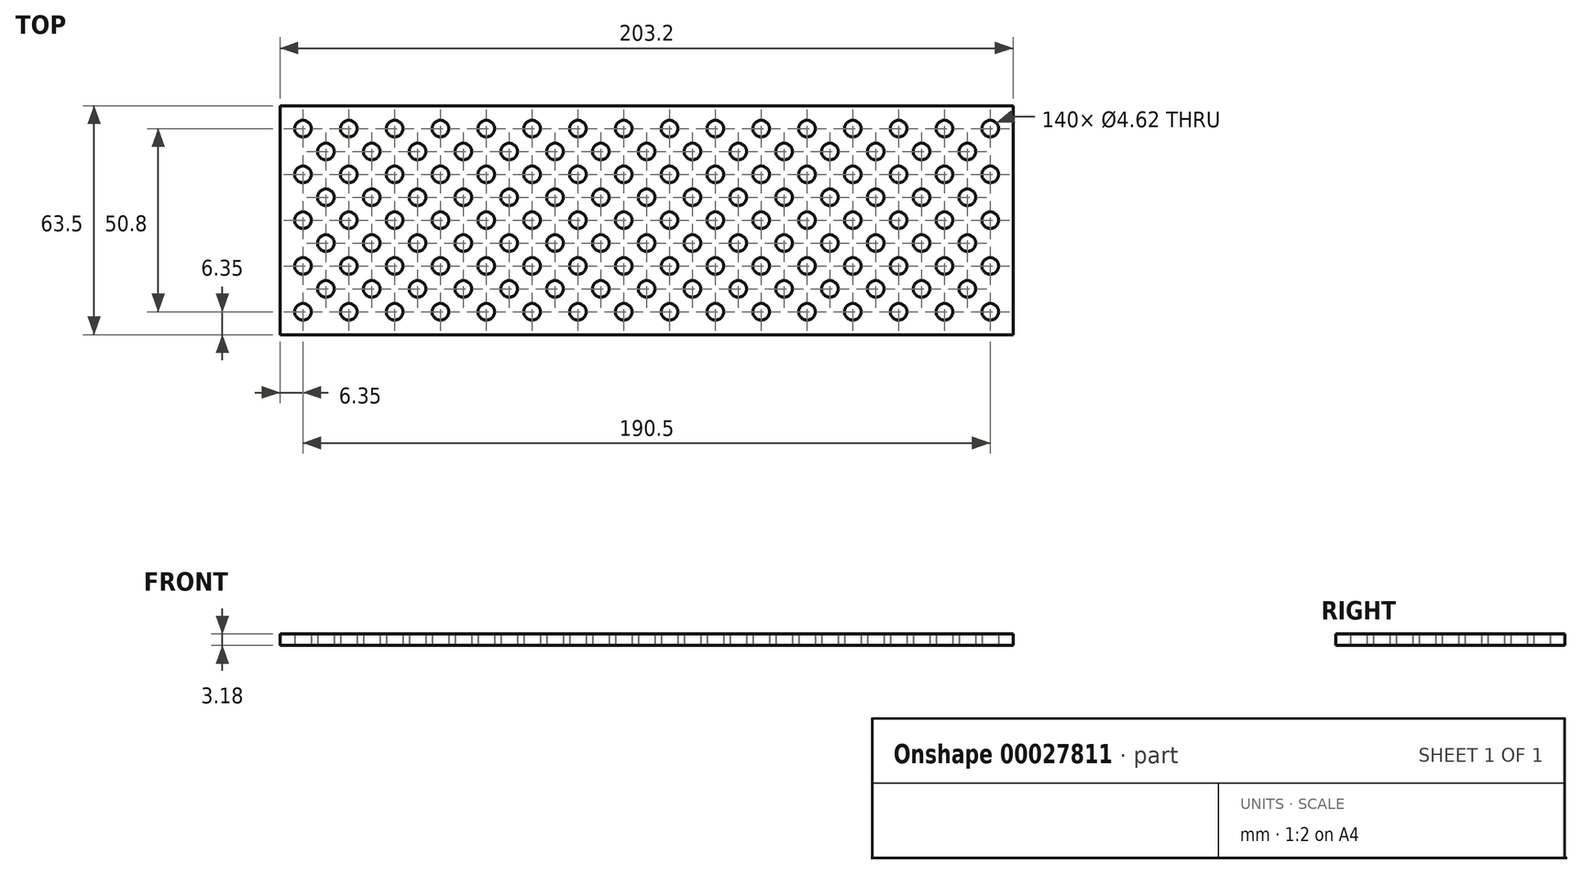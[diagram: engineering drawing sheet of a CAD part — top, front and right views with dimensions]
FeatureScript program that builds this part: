
annotation { "Feature Type Name" : "Feature", "Feature Type Description" : "" }
export const myFeature = defineFeature(function(context is Context, id is Id, definition is map)
    precondition{}
    {
        {
            var Q0;
            Q0=qCreatedBy(makeId("Top.planeOp"),FACE);
            var sketch = newSketch(context, id + "F0", { "sketchPlane" : qUnion([Q0])});
            skLineSegment(sketch, "E0.bottom", {"start": v(0, 0) * mm, "end": v(203.2, 0) * mm});
            skLineSegment(sketch, "E0.top", {"start": v(0, 63.5) * mm, "end": v(203.2, 63.5) * mm});
            skLineSegment(sketch, "E0.left", {"start": v(0, 0) * mm, "end": v(0, 63.5) * mm});
            skLineSegment(sketch, "E0.right", {"start": v(203.2, 0) * mm, "end": v(203.2, 63.5) * mm});
            skPoint(sketch, "E1", {"position": v(4.04, 4.04) * mm});
            skCircle(sketch, "E2", {"center": v(6.35, 6.35) * mm, "radius": 2.31 * mm});
            skCircle(sketch, "E3.0.1.0", {"center": v(6.35, 19.05) * mm, "radius": 2.31 * mm});
            skCircle(sketch, "E3.0.2.0", {"center": v(6.35, 31.75) * mm, "radius": 2.31 * mm});
            skCircle(sketch, "E3.0.3.0", {"center": v(6.35, 44.45) * mm, "radius": 2.31 * mm});
            skCircle(sketch, "E3.0.4.0", {"center": v(6.35, 57.15) * mm, "radius": 2.31 * mm});
            skCircle(sketch, "E3.1.0.0", {"center": v(19.05, 6.35) * mm, "radius": 2.31 * mm});
            skCircle(sketch, "E3.1.1.0", {"center": v(19.05, 19.05) * mm, "radius": 2.31 * mm});
            skCircle(sketch, "E3.1.2.0", {"center": v(19.05, 31.75) * mm, "radius": 2.31 * mm});
            skCircle(sketch, "E3.1.3.0", {"center": v(19.05, 44.45) * mm, "radius": 2.31 * mm});
            skCircle(sketch, "E3.1.4.0", {"center": v(19.05, 57.15) * mm, "radius": 2.31 * mm});
            skCircle(sketch, "E3.2.0.0", {"center": v(31.75, 6.35) * mm, "radius": 2.31 * mm});
            skCircle(sketch, "E3.2.1.0", {"center": v(31.75, 19.05) * mm, "radius": 2.31 * mm});
            skCircle(sketch, "E3.2.2.0", {"center": v(31.75, 31.75) * mm, "radius": 2.31 * mm});
            skCircle(sketch, "E3.2.3.0", {"center": v(31.75, 44.45) * mm, "radius": 2.31 * mm});
            skCircle(sketch, "E3.2.4.0", {"center": v(31.75, 57.15) * mm, "radius": 2.31 * mm});
            skCircle(sketch, "E3.3.0.0", {"center": v(44.45, 6.35) * mm, "radius": 2.31 * mm});
            skCircle(sketch, "E3.3.1.0", {"center": v(44.45, 19.05) * mm, "radius": 2.31 * mm});
            skCircle(sketch, "E3.3.2.0", {"center": v(44.45, 31.75) * mm, "radius": 2.31 * mm});
            skCircle(sketch, "E3.3.3.0", {"center": v(44.45, 44.45) * mm, "radius": 2.31 * mm});
            skCircle(sketch, "E3.3.4.0", {"center": v(44.45, 57.15) * mm, "radius": 2.31 * mm});
            skCircle(sketch, "E3.4.0.0", {"center": v(57.15, 6.35) * mm, "radius": 2.31 * mm});
            skCircle(sketch, "E3.4.1.0", {"center": v(57.15, 19.05) * mm, "radius": 2.31 * mm});
            skCircle(sketch, "E3.4.2.0", {"center": v(57.15, 31.75) * mm, "radius": 2.31 * mm});
            skCircle(sketch, "E3.4.3.0", {"center": v(57.15, 44.45) * mm, "radius": 2.31 * mm});
            skCircle(sketch, "E3.4.4.0", {"center": v(57.15, 57.15) * mm, "radius": 2.31 * mm});
            skCircle(sketch, "E3.5.0.0", {"center": v(69.85, 6.35) * mm, "radius": 2.31 * mm});
            skCircle(sketch, "E3.5.1.0", {"center": v(69.85, 19.05) * mm, "radius": 2.31 * mm});
            skCircle(sketch, "E3.5.2.0", {"center": v(69.85, 31.75) * mm, "radius": 2.31 * mm});
            skCircle(sketch, "E3.5.3.0", {"center": v(69.85, 44.45) * mm, "radius": 2.31 * mm});
            skCircle(sketch, "E3.5.4.0", {"center": v(69.85, 57.15) * mm, "radius": 2.31 * mm});
            skCircle(sketch, "E3.6.0.0", {"center": v(82.55, 6.35) * mm, "radius": 2.31 * mm});
            skCircle(sketch, "E3.6.1.0", {"center": v(82.55, 19.05) * mm, "radius": 2.31 * mm});
            skCircle(sketch, "E3.6.2.0", {"center": v(82.55, 31.75) * mm, "radius": 2.31 * mm});
            skCircle(sketch, "E3.6.3.0", {"center": v(82.55, 44.45) * mm, "radius": 2.31 * mm});
            skCircle(sketch, "E3.6.4.0", {"center": v(82.55, 57.15) * mm, "radius": 2.31 * mm});
            skCircle(sketch, "E3.7.0.0", {"center": v(95.25, 6.35) * mm, "radius": 2.31 * mm});
            skCircle(sketch, "E3.7.1.0", {"center": v(95.25, 19.05) * mm, "radius": 2.31 * mm});
            skCircle(sketch, "E3.7.2.0", {"center": v(95.25, 31.75) * mm, "radius": 2.31 * mm});
            skCircle(sketch, "E3.7.3.0", {"center": v(95.25, 44.45) * mm, "radius": 2.31 * mm});
            skCircle(sketch, "E3.7.4.0", {"center": v(95.25, 57.15) * mm, "radius": 2.31 * mm});
            skCircle(sketch, "E3.8.0.0", {"center": v(107.95, 6.35) * mm, "radius": 2.31 * mm});
            skCircle(sketch, "E3.8.1.0", {"center": v(107.95, 19.05) * mm, "radius": 2.31 * mm});
            skCircle(sketch, "E3.8.2.0", {"center": v(107.95, 31.75) * mm, "radius": 2.31 * mm});
            skCircle(sketch, "E3.8.3.0", {"center": v(107.95, 44.45) * mm, "radius": 2.31 * mm});
            skCircle(sketch, "E3.8.4.0", {"center": v(107.95, 57.15) * mm, "radius": 2.31 * mm});
            skCircle(sketch, "E3.9.0.0", {"center": v(120.65, 6.35) * mm, "radius": 2.31 * mm});
            skCircle(sketch, "E3.9.1.0", {"center": v(120.65, 19.05) * mm, "radius": 2.31 * mm});
            skCircle(sketch, "E3.9.2.0", {"center": v(120.65, 31.75) * mm, "radius": 2.31 * mm});
            skCircle(sketch, "E3.9.3.0", {"center": v(120.65, 44.45) * mm, "radius": 2.31 * mm});
            skCircle(sketch, "E3.9.4.0", {"center": v(120.65, 57.15) * mm, "radius": 2.31 * mm});
            skCircle(sketch, "E3.10.0.0", {"center": v(133.35, 6.35) * mm, "radius": 2.31 * mm});
            skCircle(sketch, "E3.10.1.0", {"center": v(133.35, 19.05) * mm, "radius": 2.31 * mm});
            skCircle(sketch, "E3.10.2.0", {"center": v(133.35, 31.75) * mm, "radius": 2.31 * mm});
            skCircle(sketch, "E3.10.3.0", {"center": v(133.35, 44.45) * mm, "radius": 2.31 * mm});
            skCircle(sketch, "E3.10.4.0", {"center": v(133.35, 57.15) * mm, "radius": 2.31 * mm});
            skCircle(sketch, "E3.11.0.0", {"center": v(146.05, 6.35) * mm, "radius": 2.31 * mm});
            skCircle(sketch, "E3.11.1.0", {"center": v(146.05, 19.05) * mm, "radius": 2.31 * mm});
            skCircle(sketch, "E3.11.2.0", {"center": v(146.05, 31.75) * mm, "radius": 2.31 * mm});
            skCircle(sketch, "E3.11.3.0", {"center": v(146.05, 44.45) * mm, "radius": 2.31 * mm});
            skCircle(sketch, "E3.11.4.0", {"center": v(146.05, 57.15) * mm, "radius": 2.31 * mm});
            skCircle(sketch, "E3.12.0.0", {"center": v(158.75, 6.35) * mm, "radius": 2.31 * mm});
            skCircle(sketch, "E3.12.1.0", {"center": v(158.75, 19.05) * mm, "radius": 2.31 * mm});
            skCircle(sketch, "E3.12.2.0", {"center": v(158.75, 31.75) * mm, "radius": 2.31 * mm});
            skCircle(sketch, "E3.12.3.0", {"center": v(158.75, 44.45) * mm, "radius": 2.31 * mm});
            skCircle(sketch, "E3.12.4.0", {"center": v(158.75, 57.15) * mm, "radius": 2.31 * mm});
            skCircle(sketch, "E3.13.0.0", {"center": v(171.45, 6.35) * mm, "radius": 2.31 * mm});
            skCircle(sketch, "E3.13.1.0", {"center": v(171.45, 19.05) * mm, "radius": 2.31 * mm});
            skCircle(sketch, "E3.13.2.0", {"center": v(171.45, 31.75) * mm, "radius": 2.31 * mm});
            skCircle(sketch, "E3.13.3.0", {"center": v(171.45, 44.45) * mm, "radius": 2.31 * mm});
            skCircle(sketch, "E3.13.4.0", {"center": v(171.45, 57.15) * mm, "radius": 2.31 * mm});
            skCircle(sketch, "E3.14.0.0", {"center": v(184.15, 6.35) * mm, "radius": 2.31 * mm});
            skCircle(sketch, "E3.14.1.0", {"center": v(184.15, 19.05) * mm, "radius": 2.31 * mm});
            skCircle(sketch, "E3.14.2.0", {"center": v(184.15, 31.75) * mm, "radius": 2.31 * mm});
            skCircle(sketch, "E3.14.3.0", {"center": v(184.15, 44.45) * mm, "radius": 2.31 * mm});
            skCircle(sketch, "E3.14.4.0", {"center": v(184.15, 57.15) * mm, "radius": 2.31 * mm});
            skCircle(sketch, "E3.15.0.0", {"center": v(196.85, 6.35) * mm, "radius": 2.31 * mm});
            skCircle(sketch, "E3.15.1.0", {"center": v(196.85, 19.05) * mm, "radius": 2.31 * mm});
            skCircle(sketch, "E3.15.2.0", {"center": v(196.85, 31.75) * mm, "radius": 2.31 * mm});
            skCircle(sketch, "E3.15.3.0", {"center": v(196.85, 44.45) * mm, "radius": 2.31 * mm});
            skCircle(sketch, "E3.15.4.0", {"center": v(196.85, 57.15) * mm, "radius": 2.31 * mm});
            skLineSegment(sketch, "E3.direction1", {"start": v(6.35, 6.35) * mm, "end": v(19.05, 6.35) * mm, "construction": true});
            skLineSegment(sketch, "E3.direction2", {"start": v(6.35, 6.35) * mm, "end": v(6.35, 19.05) * mm, "construction": true});
            skCircle(sketch, "E4", {"center": v(12.7, 12.7) * mm, "radius": 2.31 * mm});
            skCircle(sketch, "E5.0.1.0", {"center": v(12.7, 25.4) * mm, "radius": 2.31 * mm});
            skCircle(sketch, "E5.0.2.0", {"center": v(12.7, 38.1) * mm, "radius": 2.31 * mm});
            skCircle(sketch, "E5.0.3.0", {"center": v(12.7, 50.8) * mm, "radius": 2.31 * mm});
            skCircle(sketch, "E5.1.0.0", {"center": v(25.4, 12.7) * mm, "radius": 2.31 * mm});
            skCircle(sketch, "E5.1.1.0", {"center": v(25.4, 25.4) * mm, "radius": 2.31 * mm});
            skCircle(sketch, "E5.1.2.0", {"center": v(25.4, 38.1) * mm, "radius": 2.31 * mm});
            skCircle(sketch, "E5.1.3.0", {"center": v(25.4, 50.8) * mm, "radius": 2.31 * mm});
            skCircle(sketch, "E5.2.0.0", {"center": v(38.1, 12.7) * mm, "radius": 2.31 * mm});
            skCircle(sketch, "E5.2.1.0", {"center": v(38.1, 25.4) * mm, "radius": 2.31 * mm});
            skCircle(sketch, "E5.2.2.0", {"center": v(38.1, 38.1) * mm, "radius": 2.31 * mm});
            skCircle(sketch, "E5.2.3.0", {"center": v(38.1, 50.8) * mm, "radius": 2.31 * mm});
            skCircle(sketch, "E5.3.0.0", {"center": v(50.8, 12.7) * mm, "radius": 2.31 * mm});
            skCircle(sketch, "E5.3.1.0", {"center": v(50.8, 25.4) * mm, "radius": 2.31 * mm});
            skCircle(sketch, "E5.3.2.0", {"center": v(50.8, 38.1) * mm, "radius": 2.31 * mm});
            skCircle(sketch, "E5.3.3.0", {"center": v(50.8, 50.8) * mm, "radius": 2.31 * mm});
            skCircle(sketch, "E5.4.0.0", {"center": v(63.5, 12.7) * mm, "radius": 2.31 * mm});
            skCircle(sketch, "E5.4.1.0", {"center": v(63.5, 25.4) * mm, "radius": 2.31 * mm});
            skCircle(sketch, "E5.4.2.0", {"center": v(63.5, 38.1) * mm, "radius": 2.31 * mm});
            skCircle(sketch, "E5.4.3.0", {"center": v(63.5, 50.8) * mm, "radius": 2.31 * mm});
            skCircle(sketch, "E5.5.0.0", {"center": v(76.2, 12.7) * mm, "radius": 2.31 * mm});
            skCircle(sketch, "E5.5.1.0", {"center": v(76.2, 25.4) * mm, "radius": 2.31 * mm});
            skCircle(sketch, "E5.5.2.0", {"center": v(76.2, 38.1) * mm, "radius": 2.31 * mm});
            skCircle(sketch, "E5.5.3.0", {"center": v(76.2, 50.8) * mm, "radius": 2.31 * mm});
            skCircle(sketch, "E5.6.0.0", {"center": v(88.9, 12.7) * mm, "radius": 2.31 * mm});
            skCircle(sketch, "E5.6.1.0", {"center": v(88.9, 25.4) * mm, "radius": 2.31 * mm});
            skCircle(sketch, "E5.6.2.0", {"center": v(88.9, 38.1) * mm, "radius": 2.31 * mm});
            skCircle(sketch, "E5.6.3.0", {"center": v(88.9, 50.8) * mm, "radius": 2.31 * mm});
            skCircle(sketch, "E5.7.0.0", {"center": v(101.6, 12.7) * mm, "radius": 2.31 * mm});
            skCircle(sketch, "E5.7.1.0", {"center": v(101.6, 25.4) * mm, "radius": 2.31 * mm});
            skCircle(sketch, "E5.7.2.0", {"center": v(101.6, 38.1) * mm, "radius": 2.31 * mm});
            skCircle(sketch, "E5.7.3.0", {"center": v(101.6, 50.8) * mm, "radius": 2.31 * mm});
            skCircle(sketch, "E5.8.0.0", {"center": v(114.3, 12.7) * mm, "radius": 2.31 * mm});
            skCircle(sketch, "E5.8.1.0", {"center": v(114.3, 25.4) * mm, "radius": 2.31 * mm});
            skCircle(sketch, "E5.8.2.0", {"center": v(114.3, 38.1) * mm, "radius": 2.31 * mm});
            skCircle(sketch, "E5.8.3.0", {"center": v(114.3, 50.8) * mm, "radius": 2.31 * mm});
            skCircle(sketch, "E5.9.0.0", {"center": v(127, 12.7) * mm, "radius": 2.31 * mm});
            skCircle(sketch, "E5.9.1.0", {"center": v(127, 25.4) * mm, "radius": 2.31 * mm});
            skCircle(sketch, "E5.9.2.0", {"center": v(127, 38.1) * mm, "radius": 2.31 * mm});
            skCircle(sketch, "E5.9.3.0", {"center": v(127, 50.8) * mm, "radius": 2.31 * mm});
            skCircle(sketch, "E5.10.0.0", {"center": v(139.7, 12.7) * mm, "radius": 2.31 * mm});
            skCircle(sketch, "E5.10.1.0", {"center": v(139.7, 25.4) * mm, "radius": 2.31 * mm});
            skCircle(sketch, "E5.10.2.0", {"center": v(139.7, 38.1) * mm, "radius": 2.31 * mm});
            skCircle(sketch, "E5.10.3.0", {"center": v(139.7, 50.8) * mm, "radius": 2.31 * mm});
            skCircle(sketch, "E5.11.0.0", {"center": v(152.4, 12.7) * mm, "radius": 2.31 * mm});
            skCircle(sketch, "E5.11.1.0", {"center": v(152.4, 25.4) * mm, "radius": 2.31 * mm});
            skCircle(sketch, "E5.11.2.0", {"center": v(152.4, 38.1) * mm, "radius": 2.31 * mm});
            skCircle(sketch, "E5.11.3.0", {"center": v(152.4, 50.8) * mm, "radius": 2.31 * mm});
            skCircle(sketch, "E5.12.0.0", {"center": v(165.1, 12.7) * mm, "radius": 2.31 * mm});
            skCircle(sketch, "E5.12.1.0", {"center": v(165.1, 25.4) * mm, "radius": 2.31 * mm});
            skCircle(sketch, "E5.12.2.0", {"center": v(165.1, 38.1) * mm, "radius": 2.31 * mm});
            skCircle(sketch, "E5.12.3.0", {"center": v(165.1, 50.8) * mm, "radius": 2.31 * mm});
            skCircle(sketch, "E5.13.0.0", {"center": v(177.8, 12.7) * mm, "radius": 2.31 * mm});
            skCircle(sketch, "E5.13.1.0", {"center": v(177.8, 25.4) * mm, "radius": 2.31 * mm});
            skCircle(sketch, "E5.13.2.0", {"center": v(177.8, 38.1) * mm, "radius": 2.31 * mm});
            skCircle(sketch, "E5.13.3.0", {"center": v(177.8, 50.8) * mm, "radius": 2.31 * mm});
            skCircle(sketch, "E5.14.0.0", {"center": v(190.5, 12.7) * mm, "radius": 2.31 * mm});
            skCircle(sketch, "E5.14.1.0", {"center": v(190.5, 25.4) * mm, "radius": 2.31 * mm});
            skCircle(sketch, "E5.14.2.0", {"center": v(190.5, 38.1) * mm, "radius": 2.31 * mm});
            skCircle(sketch, "E5.14.3.0", {"center": v(190.5, 50.8) * mm, "radius": 2.31 * mm});
            skLineSegment(sketch, "E5.direction1", {"start": v(12.7, 12.7) * mm, "end": v(25.4, 12.7) * mm, "construction": true});
            skLineSegment(sketch, "E5.direction2", {"start": v(12.7, 12.7) * mm, "end": v(12.7, 25.4) * mm, "construction": true});
            skSolve(sketch);
        }
        {
            var Q0;
            Q0 = qSketchRegion(id + "F0", true);
            extrude(context, id + "F1", {"entities" : qUnion([Q0]), "depth" : 3.17 * mm});
        }
    });
